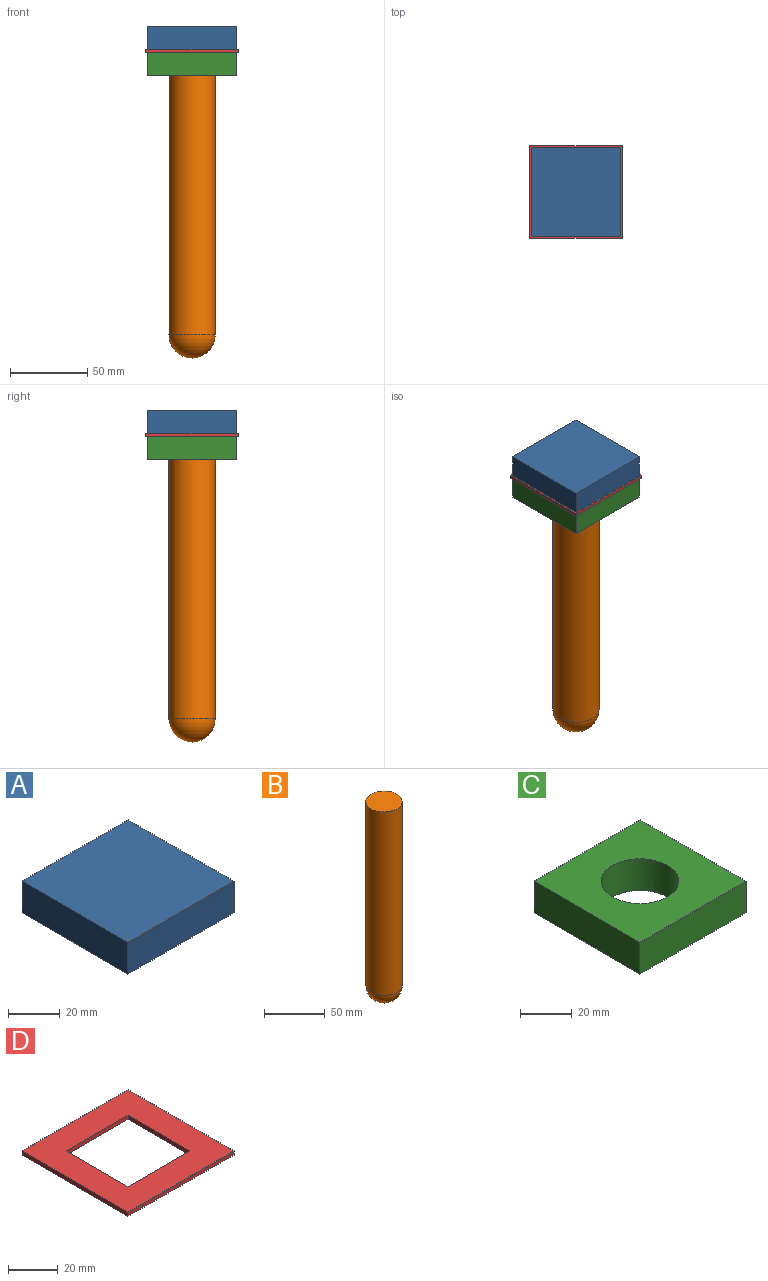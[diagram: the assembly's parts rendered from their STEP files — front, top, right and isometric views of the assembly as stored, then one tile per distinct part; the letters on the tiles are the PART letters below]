
ASSEMBLY  parts=4 mates=3
PART A: 6 faces, bbox 58x58x15 mm
  f0: plane 58x15mm, normal (0,-1,0), area 870mm2, adj f1,f3,f4,f5
  f1: plane 58x15mm, normal (1,0,0), area 870mm2, adj f0,f2,f4,f5
  f2: plane 58x15mm, normal (0,1,0), area 870mm2, adj f1,f3,f4,f5
  f3: plane 58x15mm, normal (-1,0,0), area 870mm2, adj f0,f2,f4,f5
  f4: plane 58x58mm, normal (0,0,1), area 3364mm2, adj f0,f1,f2,f3
  f5: plane 58x58mm, normal (0,0,-1), area 3364mm2, adj f0,f1,f2,f3
PART B: 3 faces, bbox 30x30x200 mm
  f0: cylinder r=15mm len=185mm, axis (0,0,1), area 17435.8mm2, adj f1,f2
  f1: plane 30x30mm, normal (0,0,1), area 706.9mm2, adj f0
  f2: sphere r=15mm, area 1413.7mm2, adj f0
PART C: 7 faces, bbox 58x58x15 mm
  f0: plane 58x15mm, normal (0,-1,0), area 870mm2, adj f1,f3,f4,f5
  f1: plane 58x15mm, normal (1,0,0), area 870mm2, adj f0,f2,f4,f5
  f2: plane 58x15mm, normal (0,1,0), area 870mm2, adj f1,f3,f4,f5
  f3: plane 58x15mm, normal (-1,0,0), area 870mm2, adj f0,f2,f4,f5
  f4: plane 58x58mm, normal (0,0,1), area 2657.1mm2, adj f0,f1,f2,f3,f6
  f5: plane 58x58mm, normal (0,0,-1), area 2657.1mm2, adj f0,f1,f2,f3,f6
  f6: cylinder r=15mm len=30mm, axis (0,0,-1), area 1413.7mm2, adj f4,f5
PART D: 10 faces, bbox 60x60x2 mm
  f0: plane 60x2mm, normal (0,-1,0), area 120mm2, adj f1,f7,f8,f9
  f1: plane 60x2mm, normal (1,0,0), area 120mm2, adj f0,f2,f8,f9
  f2: plane 60x2mm, normal (0,1,0), area 120mm2, adj f1,f7,f8,f9
  f3: plane 35x2mm, normal (-1,0,0), area 70mm2, adj f4,f6,f8,f9
  f4: plane 35x2mm, normal (0,1,0), area 70mm2, adj f3,f5,f8,f9
  f5: plane 35x2mm, normal (1,0,0), area 70mm2, adj f4,f6,f8,f9
  f6: plane 35x2mm, normal (0,-1,0), area 70mm2, adj f3,f5,f8,f9
  f7: plane 60x2mm, normal (-1,0,0), area 120mm2, adj f0,f2,f8,f9
  f8: plane 60x60mm, normal (0,0,1), area 2375mm2, adj f0,f1,f2,f3,f4,f5,f6,f7
  f9: plane 60x60mm, normal (0,0,-1), area 2375mm2, adj f0,f1,f2,f3,f4,f5,f6,f7
PLACE A at identity
PLACE B at identity fixed
PLACE C t=(0,0,-17)mm
PLACE D t=(0,0,-2)mm
MATE fastened B.f0 <-> A.f5  axis (0,0,1) through (0,0,0)mm
MATE fastened D.f9 <-> C.f6  axis (0,0,-1) through (0,0,-2)mm
MATE fastened A.f5 <-> D.f8  axis (0,0,-1) through (0,0,0)mm
